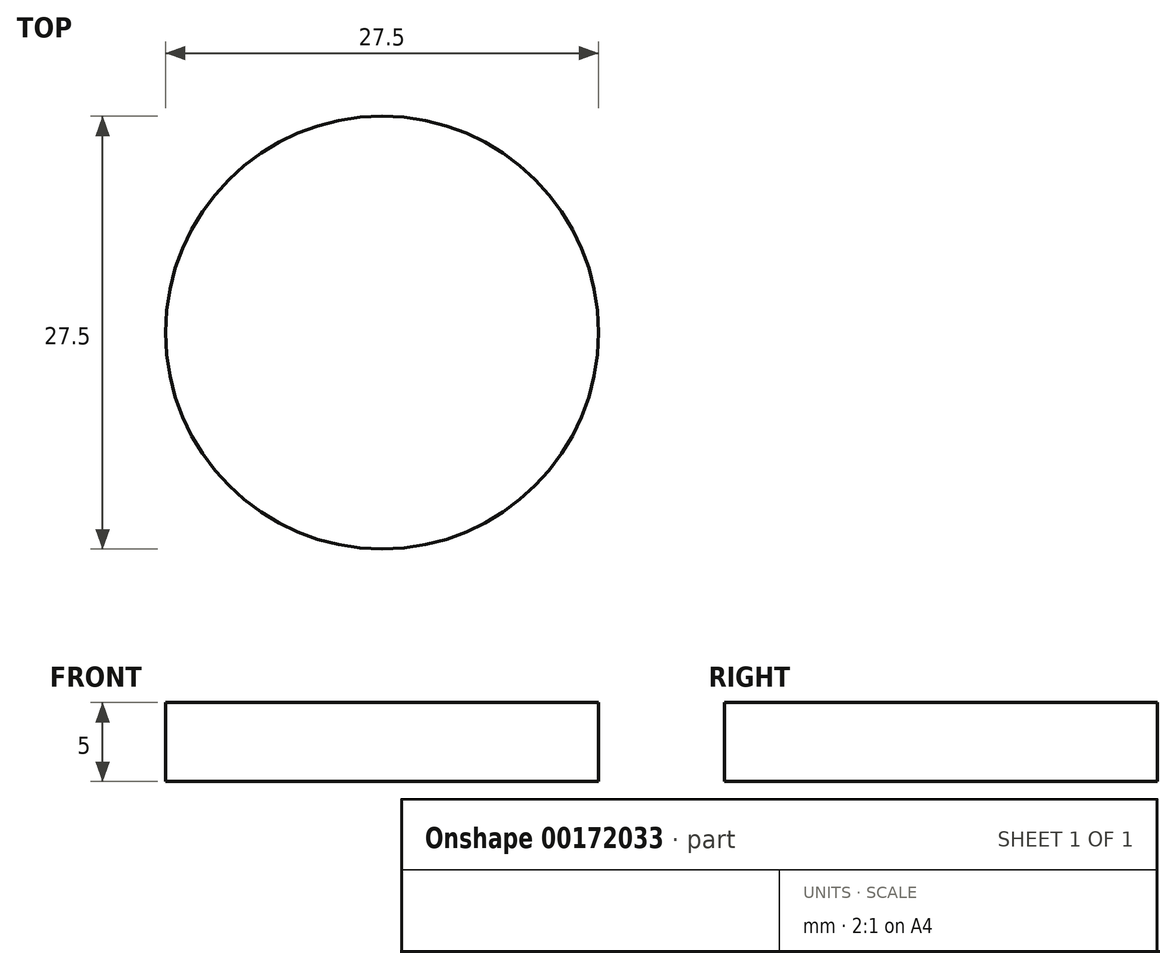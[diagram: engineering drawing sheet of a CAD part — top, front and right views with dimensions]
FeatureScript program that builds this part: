
annotation { "Feature Type Name" : "Feature", "Feature Type Description" : "" }
export const myFeature = defineFeature(function(context is Context, id is Id, definition is map)
    precondition{}
    {
        {
            var Q0;
            Q0=qCreatedBy(makeId("Top.planeOp"),FACE);
            var sketch = newSketch(context, id + "F0", { "sketchPlane" : qUnion([Q0])});
            skCircle(sketch, "E0", {"center": v(0, 0) * mm, "radius": 13.75 * mm});
            skSolve(sketch);
        }
        {
            var Q0;
            Q0=makeQuery(id+"F0.imprint","IMPRINT",FACE,{"disambiguationData":[TD([[makeQuery(id+"F0.imprint","IMPRINT",EDGE,{"derivedFrom":sQuery(id+"F0.wireOp",EDGE,"E0")}),1.0]])]});
            extrude(context, id + "F1", {"entities" : qUnion([Q0]), "depth" : 5 * mm});
        }
    });
